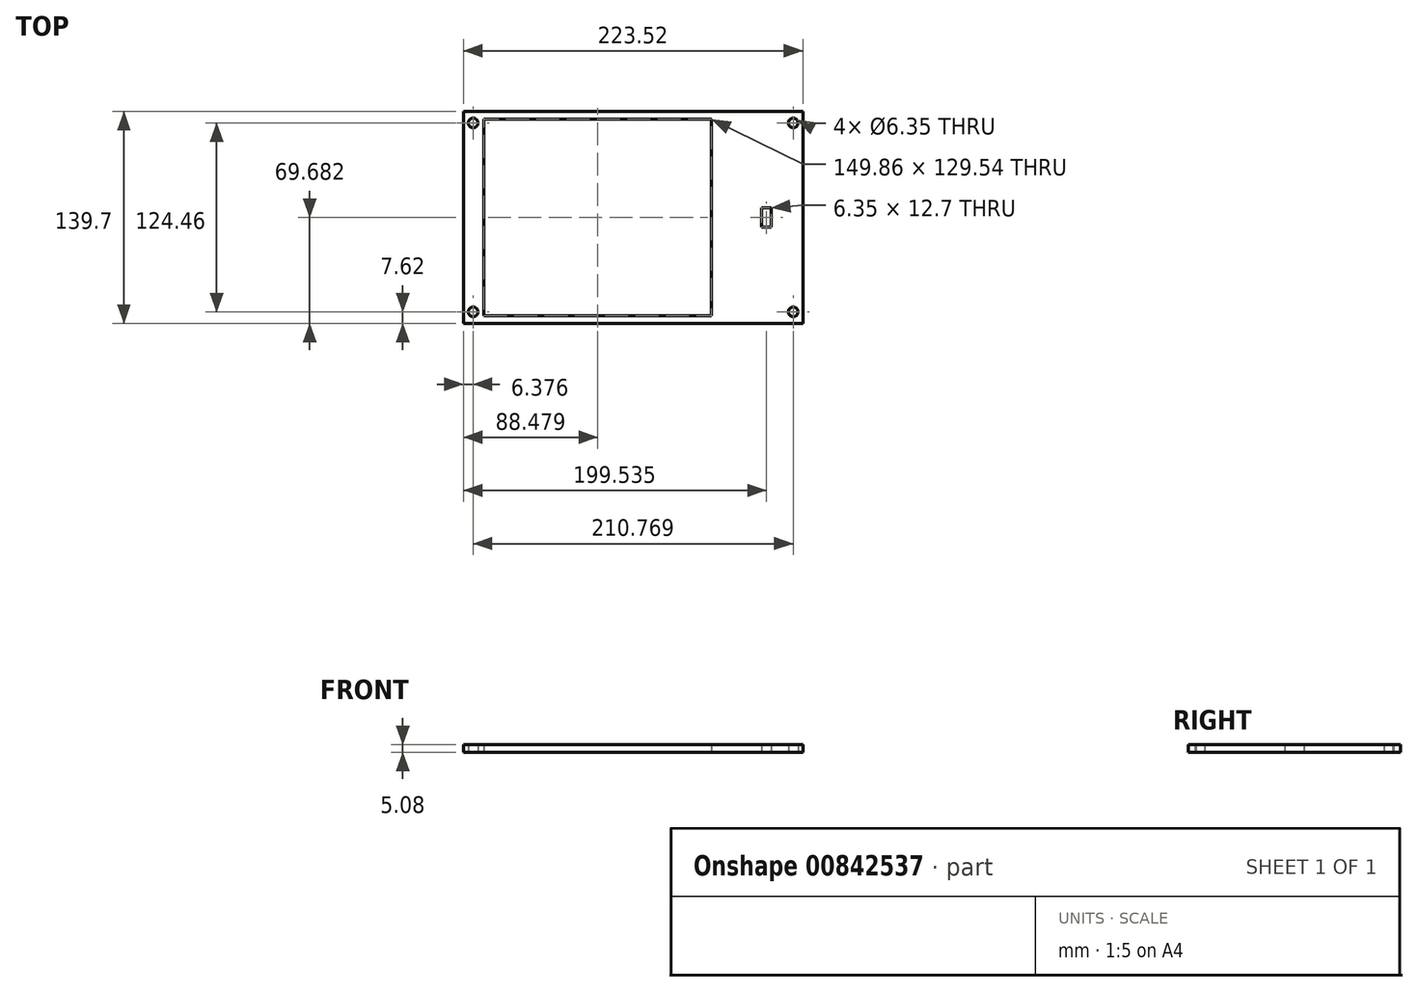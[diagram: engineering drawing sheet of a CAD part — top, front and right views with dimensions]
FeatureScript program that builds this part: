
annotation { "Feature Type Name" : "Feature", "Feature Type Description" : "" }
export const myFeature = defineFeature(function(context is Context, id is Id, definition is map)
    precondition{}
    {
        {
            var Q0;
            Q0=qCreatedBy(makeId("Top.planeOp"),FACE);
            var sketch = newSketch(context, id + "F0", { "sketchPlane" : qUnion([Q0])});
            skLineSegment(sketch, "E0.bottom", {"start": v(-196.78, 116.47) * mm, "end": v(20.81, 116.47) * mm});
            skLineSegment(sketch, "E0.top", {"start": v(-196.78, -23.23) * mm, "end": v(20.81, -23.23) * mm});
            skLineSegment(sketch, "E0.right", {"start": v(20.81, 116.47) * mm, "end": v(20.81, -23.23) * mm});
            skLineSegment(sketch, "E1.top", {"start": v(-196.78, 116.47) * mm, "end": v(-35.5, 116.47) * mm});
            skLineSegment(sketch, "E2.bottom", {"start": v(-35.5, 116.47) * mm, "end": v(-39.3, 116.47) * mm});
            skLineSegment(sketch, "E2.top", {"start": v(-35.5, 116.47) * mm, "end": v(-39.3, 116.47) * mm});
            skLineSegment(sketch, "E2.left", {"start": v(-35.5, 116.47) * mm, "end": v(-35.5, 116.47) * mm});
            skLineSegment(sketch, "E2.right", {"start": v(-39.3, 116.47) * mm, "end": v(-39.3, 116.47) * mm});
            skLineSegment(sketch, "E3", {"start": v(-196.78, 116.47) * mm, "end": v(-189.16, 116.47) * mm});
            skLineSegment(sketch, "E4.bottom", {"start": v(-189.16, 116.47) * mm, "end": v(-39.3, 116.47) * mm});
            skLineSegment(sketch, "E4.top", {"start": v(-189.16, 116.47) * mm, "end": v(-39.3, 116.47) * mm});
            skLineSegment(sketch, "E4.left", {"start": v(-189.16, 116.47) * mm, "end": v(-189.16, 116.47) * mm});
            skLineSegment(sketch, "E5.bottom", {"start": v(-189.16, 111.22) * mm, "end": v(-39.3, 111.22) * mm});
            skLineSegment(sketch, "E5.top", {"start": v(-189.16, -18.32) * mm, "end": v(-39.3, -18.32) * mm});
            skLineSegment(sketch, "E5.left", {"start": v(-189.16, 111.22) * mm, "end": v(-189.16, -18.32) * mm});
            skLineSegment(sketch, "E5.right", {"start": v(-39.3, 111.22) * mm, "end": v(-39.3, -18.32) * mm});
            skPoint(sketch, "E6.oppositeSnap0", {"position": v(-39.3, 46.45) * mm});
            skLineSegment(sketch, "E6.bottom", {"start": v(-35.5, 116.47) * mm, "end": v(15.3, 116.47) * mm});
            skLineSegment(sketch, "E7.bottom", {"start": v(-196.78, 116.47) * mm, "end": v(-202.7, 116.47) * mm});
            skLineSegment(sketch, "E7.top", {"start": v(-196.78, -23.23) * mm, "end": v(-202.7, -23.23) * mm});
            skLineSegment(sketch, "E7.right", {"start": v(-202.7, 116.47) * mm, "end": v(-202.7, -23.23) * mm});
            skLineSegment(sketch, "E8.bottom", {"start": v(-202.7, 116.47) * mm, "end": v(-195.09, 116.47) * mm});
            skLineSegment(sketch, "E8.left", {"start": v(-202.7, 116.47) * mm, "end": v(-202.7, 108.85) * mm});
            skCircle(sketch, "E9", {"center": v(-196.33, 108.85) * mm, "radius": 3.17 * mm});
            skLineSegment(sketch, "E10.bottom", {"start": v(-202.7, 116.47) * mm, "end": v(-187.47, 116.47) * mm});
            skLineSegment(sketch, "E10.left", {"start": v(-202.7, 116.47) * mm, "end": v(-202.7, 101.23) * mm});
            skLineSegment(sketch, "E11.left", {"start": v(-202.7, 101.23) * mm, "end": v(-202.7, -23.23) * mm});
            skLineSegment(sketch, "E12.bottom", {"start": v(-90.95, 111.4) * mm, "end": v(-189.16, 111.4) * mm});
            skLineSegment(sketch, "E12.top", {"start": v(-90.95, 116.47) * mm, "end": v(-187.47, 116.47) * mm});
            skLineSegment(sketch, "E13", {"start": v(-189.16, 111.4) * mm, "end": v(-189.16, 107.58) * mm});
            skPoint(sketch, "E14.visualSharp", {"position": v(-189.16, 101.23) * mm});
            skPoint(sketch, "E15.endSnap0", {"position": v(-87.98, -23.23) * mm});
            skCircle(sketch, "E16.MirrorC", {"center": v(14.43, 108.85) * mm, "radius": 3.17 * mm});
            skCircle(sketch, "E17.MirrorC", {"center": v(-196.33, -15.6) * mm, "radius": 3.17 * mm});
            skCircle(sketch, "E18.MirrorC", {"center": v(14.43, -15.6) * mm, "radius": 3.17 * mm});
            skLineSegment(sketch, "E19", {"start": v(0, 46.45) * mm, "end": v(0, 52.8) * mm});
            skLineSegment(sketch, "E20.bottom", {"start": v(0, 52.8) * mm, "end": v(-6.35, 52.8) * mm});
            skLineSegment(sketch, "E20.left", {"start": v(0, 52.8) * mm, "end": v(0, 46.45) * mm});
            skLineSegment(sketch, "E20.right", {"start": v(-6.35, 52.8) * mm, "end": v(-6.35, 46.45) * mm});
            skLineSegment(sketch, "E21.MirrorCS", {"start": v(0, 40.1) * mm, "end": v(-6.35, 40.1) * mm});
            skLineSegment(sketch, "E22.bottom", {"start": v(-6.35, 52.8) * mm, "end": v(0, 52.8) * mm});
            skLineSegment(sketch, "E22.top", {"start": v(-6.35, 40.1) * mm, "end": v(0, 40.1) * mm});
            skLineSegment(sketch, "E22.left", {"start": v(-6.35, 52.8) * mm, "end": v(-6.35, 40.1) * mm});
            skLineSegment(sketch, "E22.right", {"start": v(0, 52.8) * mm, "end": v(0, 40.1) * mm});
            skSolve(sketch);
        }
        {
            var Q0;
            Q0=qSketchRegion(id+"F0",true);
            var Q1;
            Q1=makeQuery(id+"F0.imprint","IMPRINT",FACE,{"disambiguationData":[TD([[makeQuery(id+"F0.imprint","IMPRINT",EDGE,{"derivedFrom":sQuery(id+"F0.wireOp",EDGE,"ps8PWAJg-xcaU-0UHa-hZd1-3VqYm1P8FTMH.bottom")}),-1.0]])]});
            extrude(context, id + "F1", {"entities" : qUnion([Q0, Q1]), "depth" : 5.08 * mm, "offsetDistance" : 25.4 * mm});
        }
    });
